# Revit family: ledpanelsp-z_l1222-80w-ble2-4000-al_542004091800
name_source: partatom
category: Leuchten
revit_build: Autodesk Revit 2016 (Build: 20190508_0715(x64)
units: mm (PartAtom-declared; Revit-internal decimal feet)

## family parameters
Basisbauteil = Fläche
Beim Laden mit Abzugskörper schneiden = Nein
Bemaßung runder Anschluss = Durchmesser verwenden
Gemeinsam genutzt = Nein
Lichtquelle = Nein
Raumberechnungspunkt = Nein
Teiletyp = Normal

## types (1)
- LEDPanelSp-Z L1222-80W-BLE2-4000-AL (1 x LED, 8600 lm, 4000)
    Approval mark = CE, ENEC
    Beschreibung = Special design luminaire distributes light both up and down, combining comfort and efficiency. Light up your offices and meeting rooms in an architectural way. Standard including suspension kit (2.5m) and separate aluminum colored driver housing.
    CIE Flux Codes = 46 77 94 48 100
    Color Rendering = 80
    Color Temperature = 4000
    Control Gear = Electronic ballast
    Frequency = 60 Hz
    Height = 18 mm
    Hersteller = OPPLE
    Lamp Light Flux = 8600 lm
    Lamp count = 1
    Lampe = 1 x LED
    Length = 1222 mm
    Luminous efficacy = 108 lm/W
    ModVariant = Nein
    Modell = 542004091800
    Mounting Place = Ceiling, Pole
    Mounting Type = Pendant
    Number of Poles = 1
    OnlyDefault = Ja
    Power Factor = 1
    Product Name = LEDPanelSp-Z L1222-80W-BLE2-4000-AL
    Product group = Pendant luminaire
    ProductGroupID = 9
    Protection Class = Protection class II
    Protection Degree = IP 20
    RLX_Detail_Level = 1
    RlxData = <blob elided: 92993 chars, md5=629bf602>
    Scheinlast = 80 VA
    Socket = socket
    Standby Power = 0 W
    System Light Flux = 8600 lm
    System Power = 80 W
    Typenbild = zenith.jpg
    Typenkommentare = Product without accessories
    URL = http://relux.com
    VarID = ---
    Voltage = 230 V
    Voltage Range = 220-240 V
    Vorgabe-Ansicht = 1800 mm
    Weight = 0.00 kg
    Width = 236 mm

## geometry (parser evidence)
native form markers: Blend x4, Sweep x15
no freeform markers — native parametric forms only
